# Revit family: Arper_Catifa53 Carta_chair_five-star-swivel_3151
name_source: partatom
category: Furniture
units: mm (PartAtom-declared; Revit-internal decimal feet)

## family parameters
Always vertical = Yes
Cut with Voids When Loaded = No
OmniClass Number = 23.40.20.00
OmniClass Title = General Furniture and Specialties
Room Calculation Point = No
Shared = No
Work Plane-Based = No

## types (1)
- Arper_Catifa53 Carta_chair_five-star-swivel_3151
    Armrests = No
    Arper - Weels material = Arper - generic black
    Default Elevation = 0 mm  [stored 0 ft]
    Description = Chair with polished or powdercoated aluminum five-star swivel base, mounted on self-braking castors (color matching with base) and fitted with gas height adjustment mechanism. Shell in PaperShell. Upon request steel armrests are offered in the same finishes of the base.
    Manufacturer = ARPER s.p.a.
    Model = Catifa Carta
    URL = http://www.arper.com

note: [stored X ft] marks values corroborated as IEEE doubles in the binary element streams (Revit-internal decimal feet)
